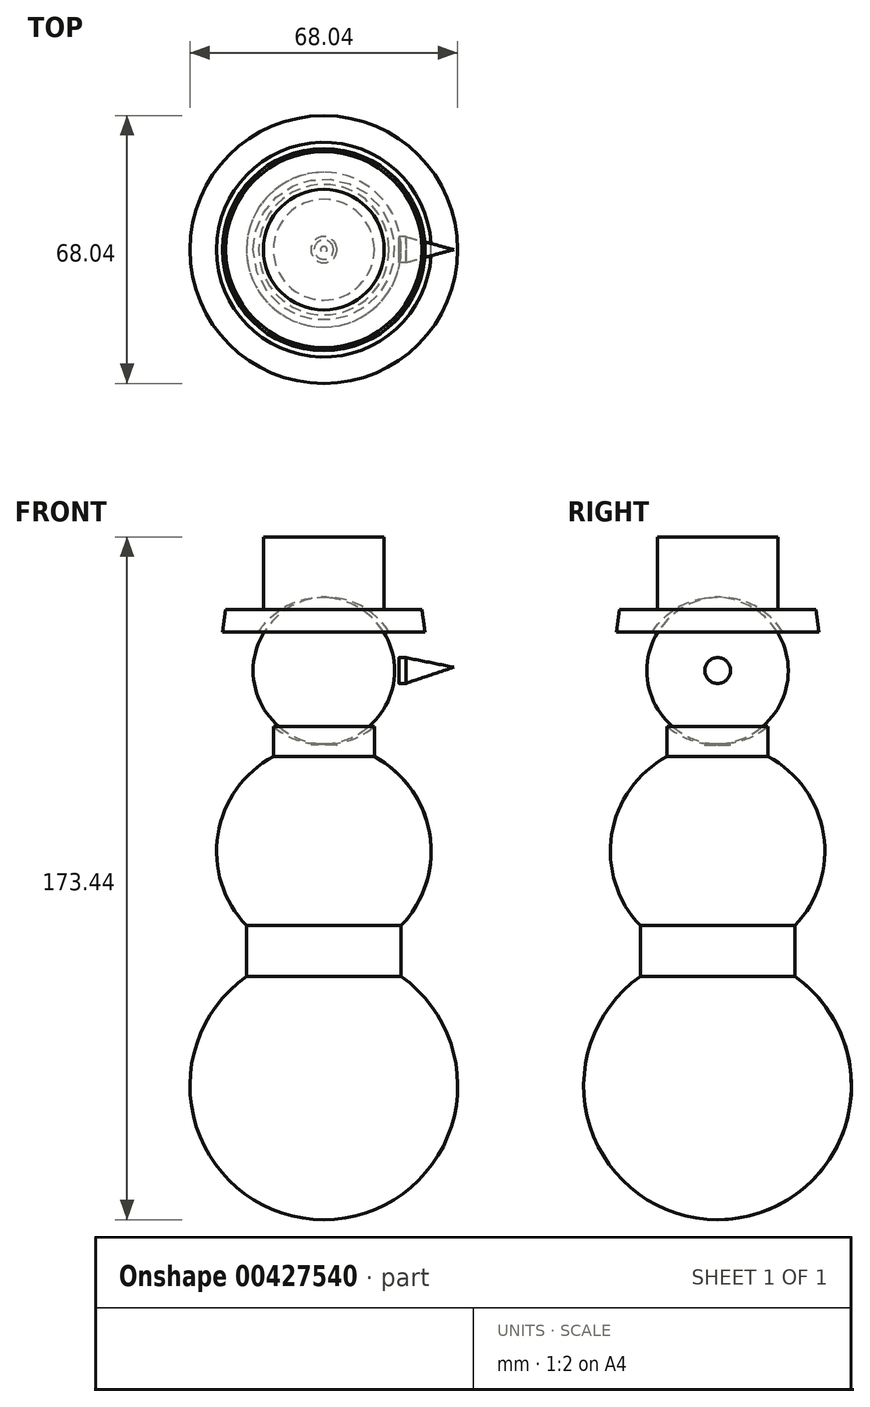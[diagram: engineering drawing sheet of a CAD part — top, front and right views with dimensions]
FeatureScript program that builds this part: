
annotation { "Feature Type Name" : "Feature", "Feature Type Description" : "" }
export const myFeature = defineFeature(function(context is Context, id is Id, definition is map)
    precondition{}
    {
        {
            var Q0;
            Q0=qCreatedBy(makeId("Right.planeOp"),FACE);
            var sketch = newSketch(context, id + "F0", { "sketchPlane" : qUnion([Q0])});
            skArc(sketch, "E0", {"start": v(0, -66.33) * mm, "mid": v(34.02, -32.31) * mm, "end": v(0, 1.7) * mm});
            skArc(sketch, "E1", {"start": v(0, 0) * mm, "mid": v(27.26, 27.26) * mm, "end": v(0, 54.52) * mm});
            skArc(sketch, "E2", {"start": v(0, 54.52) * mm, "mid": v(16.8, 63.77) * mm, "end": v(16.56, 82.96) * mm});
            skPoint(sketch, "E2.first.point", {"position": v(0, 54.52) * mm});
            skPoint(sketch, "E2.second.point", {"position": v(0, 91.8) * mm});
            skPoint(sketch, "E2.third.point", {"position": v(-17.88, 74.82) * mm});
            skLineSegment(sketch, "E3", {"start": v(12.81, 58.98) * mm, "end": v(12.81, 51.32) * mm});
            skLineSegment(sketch, "E4", {"start": v(12.81, 51.32) * mm, "end": v(0, 55.36) * mm});
            skLineSegment(sketch, "E5", {"start": v(19.65, 8.37) * mm, "end": v(19.65, -4.54) * mm});
            skLineSegment(sketch, "E6", {"start": v(0, 91.8) * mm, "end": v(0, -66.33) * mm});
            skLineSegment(sketch, "E7", {"start": v(16.56, 82.96) * mm, "end": v(25.7, 82.96) * mm});
            skLineSegment(sketch, "E8", {"start": v(25.7, 82.96) * mm, "end": v(24.93, 88.7) * mm});
            skLineSegment(sketch, "E9", {"start": v(24.93, 88.7) * mm, "end": v(15.34, 88.7) * mm});
            skLineSegment(sketch, "E10", {"start": v(15.34, 88.7) * mm, "end": v(15.34, 107.11) * mm});
            skLineSegment(sketch, "E11", {"start": v(15.34, 107.11) * mm, "end": v(0, 107.11) * mm});
            skLineSegment(sketch, "E12", {"start": v(0, 107.11) * mm, "end": v(0, 82.96) * mm});
            skSolve(sketch);
        }
        {
            var Q0;
            Q0 = qSketchRegion(id + "F0", true);
            var Q1;
            Q1=sQuery(id+"F0.wireOp",EDGE,"E6");
            revolve(context, id + "F1", {"entities" : qUnion([Q0]), "axis" : qUnion([Q1]), "revolveType" : RevolveType.FULL});
        }
        {
            var Q0;
            Q0=qCreatedBy(makeId("Right.planeOp"),FACE);
            var sketch = newSketch(context, id + "F2", { "sketchPlane" : qUnion([Q0])});
            skPoint(sketch, "E13", {"position": v(0, 73.2) * mm});
            skCircle(sketch, "E14", {"center": v(0, 73.2) * mm, "radius": 3.27 * mm});
            skSolve(sketch);
        }
        {
            var Q0;
            Q0 = qSketchRegion(id + "F2", true);
            extrude(context, id + "F3", {"entities" : qUnion([Q0]), "operationType" : NewBodyOperationType.ADD, "depth" : 20.83 * mm});
        }
        {
            var Q0;
            Q0=qCreatedBy(makeId("Right.planeOp"),FACE);
            cPlane(context, id + "F4", {"entities" : qUnion([Q0]), "cplaneType" : CPlaneType.OFFSET, "offset" : 33.02 * mm, "width" : 152.4 * mm, "height" : 152.4 * mm});
        }
        {
            var Q0;
            Q0=qCreatedBy(id+"F4.planeOp",FACE);
            var sketch = newSketch(context, id + "F5", { "sketchPlane" : qUnion([Q0])});
            skPoint(sketch, "E15", {"position": v(0, 74.04) * mm});
            skSolve(sketch);
        }
        {
            var Q0;
            Q0=makeQuery(id+"F3.opExtrude","CAP_FACE",FACE,{"disambiguationData":[OSD([sQuery(id+"F2.wireOp",EDGE,"E14")])],"isStart":false});
            var Q1;
            Q1=sQuery(id+"F5.wireOp",VERTEX,"E15");
            loft(context, id + "F6", {"sheetProfilesArray" : [{ "sheetProfileEntities" : qUnion([Q0]) }, { "sheetProfileEntities" : qUnion([Q1]) }]});
        }
    });
